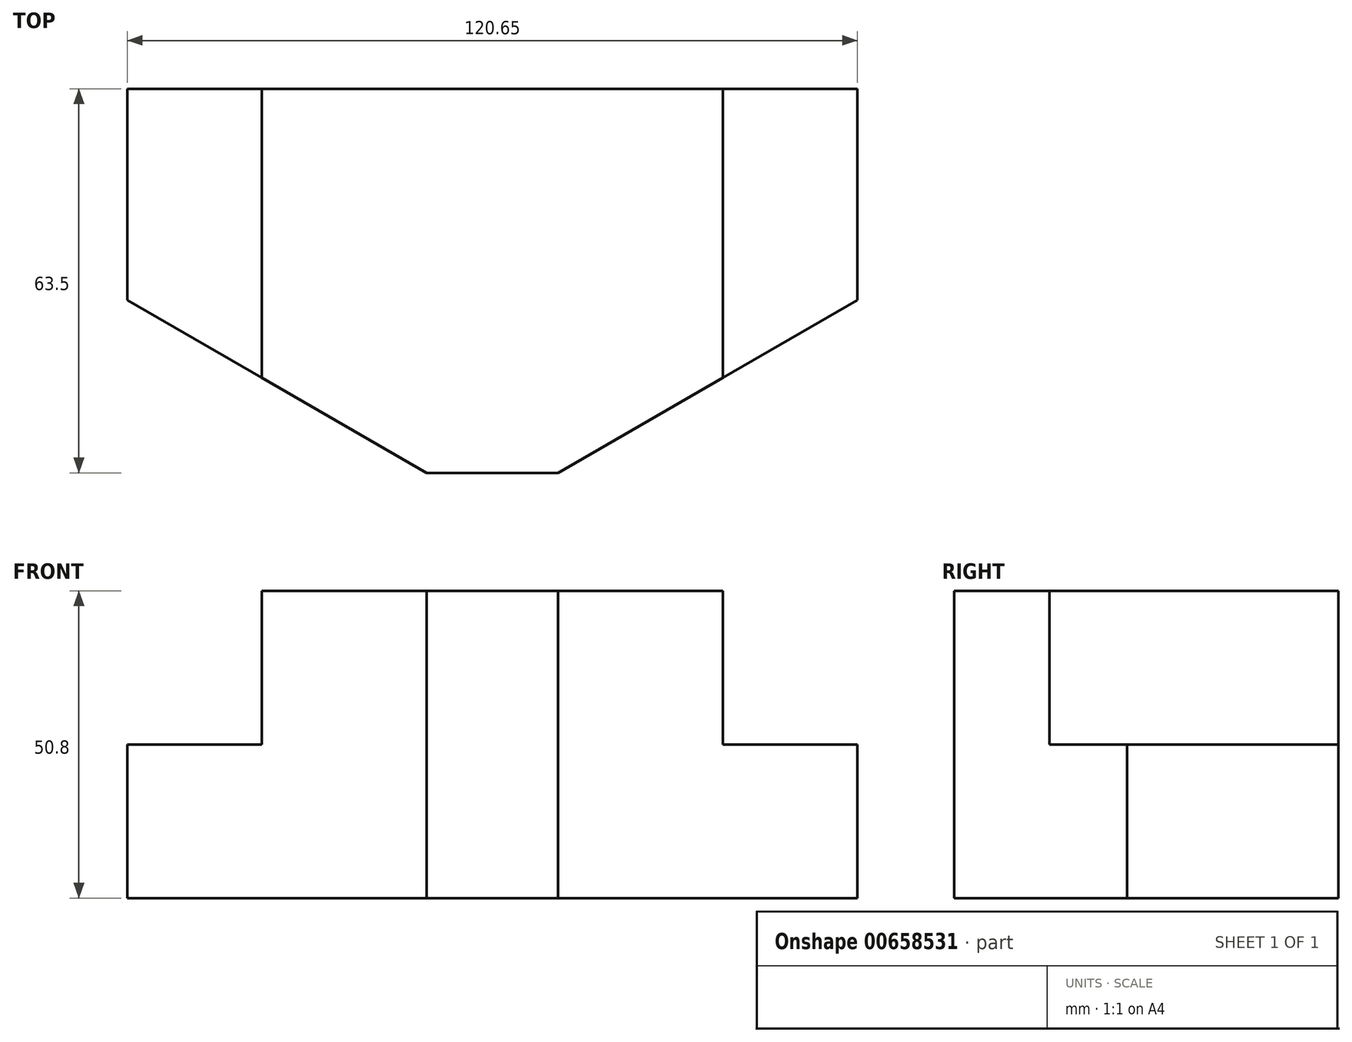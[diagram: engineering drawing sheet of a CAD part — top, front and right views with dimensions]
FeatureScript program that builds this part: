
annotation { "Feature Type Name" : "Feature", "Feature Type Description" : "" }
export const myFeature = defineFeature(function(context is Context, id is Id, definition is map)
    precondition{}
    {
        {
            var Q0;
            Q0=qCreatedBy(makeId("Top.planeOp"),FACE);
            var sketch = newSketch(context, id + "F0", { "sketchPlane" : qUnion([Q0])});
            skLineSegment(sketch, "E0", {"start": v(-90.24, 49.6) * mm, "end": v(30.4, 49.6) * mm});
            skLineSegment(sketch, "E1", {"start": v(30.4, 49.6) * mm, "end": v(30.4, 14.68) * mm});
            skLineSegment(sketch, "E2", {"start": v(-90.24, 49.6) * mm, "end": v(-90.24, 14.68) * mm});
            skLineSegment(sketch, "E3", {"start": v(-90.24, 14.68) * mm, "end": v(-90.24, -13.9) * mm, "construction": true});
            skLineSegment(sketch, "E4", {"start": v(30.4, 14.68) * mm, "end": v(30.4, -13.9) * mm, "construction": true});
            skLineSegment(sketch, "E5", {"start": v(30.4, -13.9) * mm, "end": v(-90.24, -13.9) * mm, "construction": true});
            skLineSegment(sketch, "E6", {"start": v(-90.24, 14.68) * mm, "end": v(-40.75, -13.9) * mm});
            skLineSegment(sketch, "E7", {"start": v(30.4, 14.68) * mm, "end": v(-19.08, -13.9) * mm});
            skLineSegment(sketch, "E8", {"start": v(-40.75, -13.9) * mm, "end": v(-19.08, -13.9) * mm});
            skSolve(sketch);
        }
        {
            var Q0;
            Q0=makeQuery(id+"F0.imprint","IMPRINT",FACE,{"disambiguationData":[TD([[makeQuery(id+"F0.imprint","IMPRINT",EDGE,{"derivedFrom":sQuery(id+"F0.wireOp",EDGE,"E0")}),-1.0]])]});
            extrude(context, id + "F1", {"entities" : qUnion([Q0]), "depth" : 50.8 * mm, "offsetDistance" : 25.4 * mm});
        }
        {
            var Q0;
            Q0=makeQuery(id+"F1.opExtrude","SWEPT_FACE",FACE,{"disambiguationData":[OSD([sQuery(id+"F0.wireOp",EDGE,"E0")])]});
            var sketch = newSketch(context, id + "F2", { "sketchPlane" : qUnion([Q0])});
            skLineSegment(sketch, "E9", {"start": v(-30.4, 0) * mm, "end": v(-30.4, 25.4) * mm, "construction": true});
            skLineSegment(sketch, "E10", {"start": v(-30.4, 25.4) * mm, "end": v(-8.18, 25.4) * mm});
            skLineSegment(sketch, "E11", {"start": v(-8.18, 25.4) * mm, "end": v(-8.18, 50.8) * mm});
            skLineSegment(sketch, "E12", {"start": v(-8.18, 50.8) * mm, "end": v(-30.4, 50.8) * mm});
            skLineSegment(sketch, "E13", {"start": v(-30.4, 50.8) * mm, "end": v(-30.4, 25.4) * mm});
            skLineSegment(sketch, "E14", {"start": v(90.24, 0) * mm, "end": v(90.24, 25.4) * mm, "construction": true});
            skLineSegment(sketch, "E15", {"start": v(90.24, 25.4) * mm, "end": v(68.02, 25.4) * mm});
            skLineSegment(sketch, "E16", {"start": v(68.02, 25.4) * mm, "end": v(68.02, 50.8) * mm});
            skLineSegment(sketch, "E17", {"start": v(68.02, 50.8) * mm, "end": v(90.24, 50.8) * mm});
            skLineSegment(sketch, "E18", {"start": v(90.24, 50.8) * mm, "end": v(90.24, 25.4) * mm});
            skSolve(sketch);
        }
        {
            var Q0;
            Q0=makeQuery(id+"F2.imprint","IMPRINT",FACE,{"disambiguationData":[TD([[makeQuery(id+"F2.imprint","IMPRINT",EDGE,{"derivedFrom":sQuery(id+"F2.wireOp",EDGE,"E10")}),1.0]])]});
            var Q1;
            Q1=makeQuery(id+"F2.imprint","IMPRINT",FACE,{"disambiguationData":[TD([[makeQuery(id+"F2.imprint","IMPRINT",EDGE,{"derivedFrom":sQuery(id+"F2.wireOp",EDGE,"E15")}),-1.0]])]});
            extrude(context, id + "F3", {"entities" : qUnion([Q0, Q1]), "operationType" : NewBodyOperationType.REMOVE, "oppositeDirection" : true, "depth" : 50.8 * mm, "offsetDistance" : 25.4 * mm});
        }
    });
